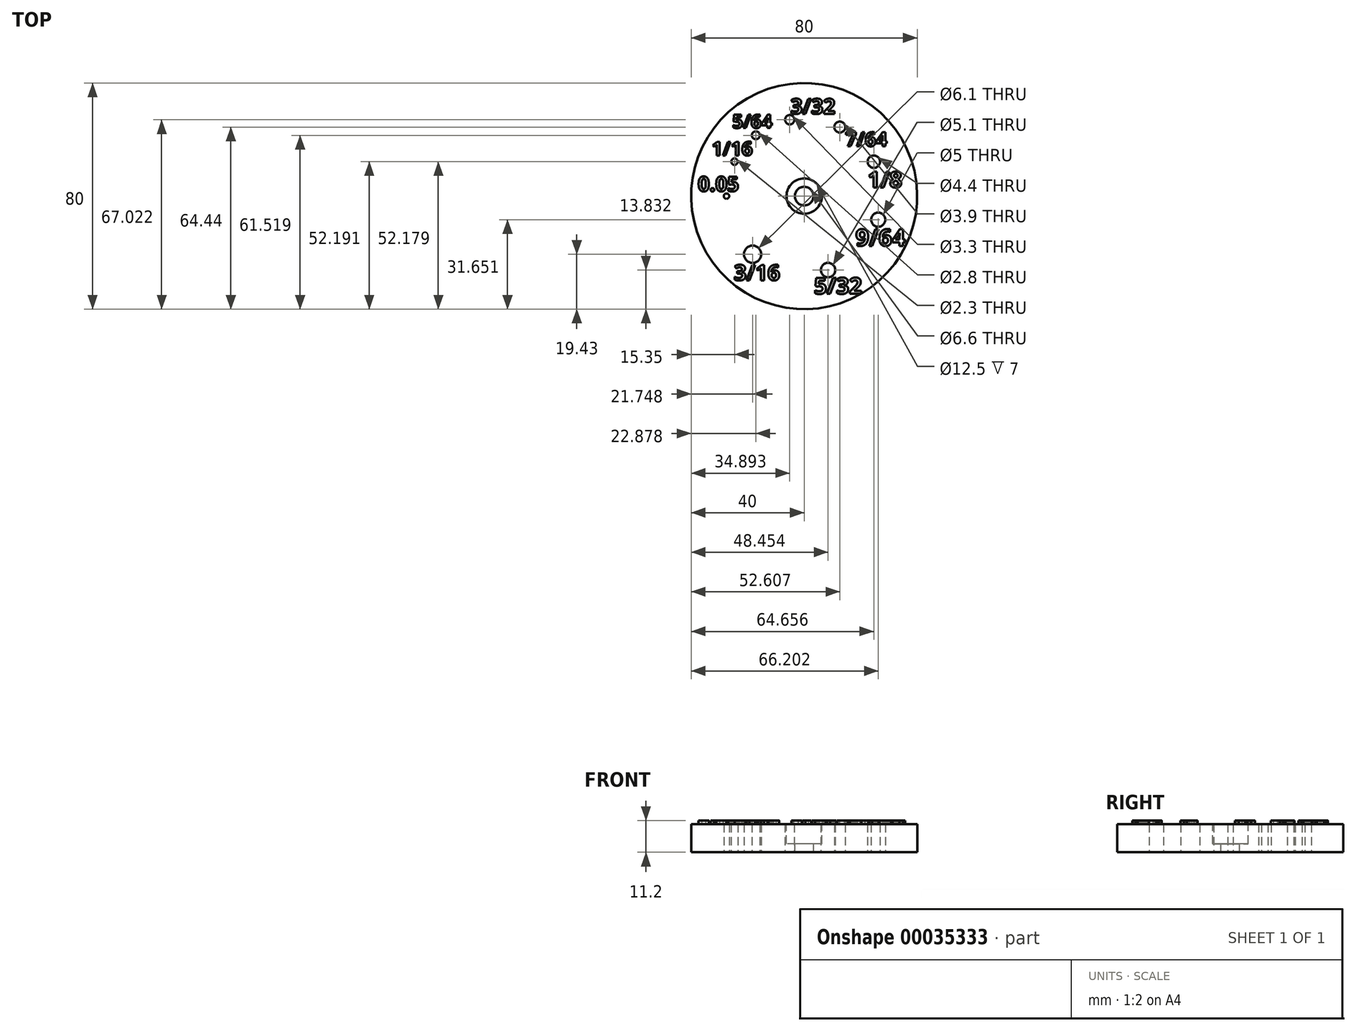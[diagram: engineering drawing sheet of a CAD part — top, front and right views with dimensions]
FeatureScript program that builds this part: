
annotation { "Feature Type Name" : "Feature", "Feature Type Description" : "" }
export const myFeature = defineFeature(function(context is Context, id is Id, definition is map)
    precondition{}
    {
        {
            var Q0;
            Q0=qCreatedBy(makeId("Top.planeOp"),FACE);
            var sketch = newSketch(context, id + "F0", { "sketchPlane" : qUnion([Q0])});
            skCircle(sketch, "E0", {"center": v(0, 0) * mm, "radius": 40 * mm});
            skCircle(sketch, "E1", {"center": v(-18.25, -20.57) * mm, "radius": 3.05 * mm});
            skCircle(sketch, "E2", {"center": v(8.45, -26.17) * mm, "radius": 2.55 * mm});
            skCircle(sketch, "E3", {"center": v(26.2, -8.35) * mm, "radius": 2.5 * mm});
            skCircle(sketch, "E4", {"center": v(24.66, 12.18) * mm, "radius": 2.2 * mm});
            skCircle(sketch, "E5", {"center": v(12.6, 24.44) * mm, "radius": 1.95 * mm});
            skCircle(sketch, "E6", {"center": v(-5.1, 27.02) * mm, "radius": 1.65 * mm});
            skCircle(sketch, "E7", {"center": v(-17.12, 21.52) * mm, "radius": 1.4 * mm});
            skCircle(sketch, "E8", {"center": v(-24.65, 12.2) * mm, "radius": 1.15 * mm});
            skCircle(sketch, "E9", {"center": v(-27.5, 0) * mm, "radius": 0.95 * mm});
            skCircle(sketch, "E10", {"center": v(0, 0) * mm, "radius": 27.5 * mm, "construction": true});
            skCircle(sketch, "E11", {"center": v(-18.25, -20.57) * mm, "radius": 13 * mm, "construction": true});
            skCircle(sketch, "E12", {"center": v(8.45, -26.17) * mm, "radius": 13 * mm, "construction": true});
            skCircle(sketch, "E13", {"center": v(26.2, -8.35) * mm, "radius": 10 * mm, "construction": true});
            skCircle(sketch, "E14", {"center": v(24.66, 12.18) * mm, "radius": 8 * mm, "construction": true});
            skCircle(sketch, "E15", {"center": v(12.6, 24.44) * mm, "radius": 7 * mm, "construction": true});
            skSolve(sketch);
        }
        {
            var Q0;
            Q0=makeQuery(id+"F0.imprint","IMPRINT",FACE,{"disambiguationData":[TD([[makeQuery(id+"F0.imprint","IMPRINT",EDGE,{"derivedFrom":sQuery(id+"F0.wireOp",EDGE,"E0")}),1.0]])]});
            extrude(context, id + "F1", {"entities" : qUnion([Q0]), "depth" : 10 * mm});
        }
        {
            var Q0;
            Q0=makeQuery(id+"F1.opExtrude","CAP_FACE",FACE,{"disambiguationData":[OSD([sQuery(id+"F0.wireOp",EDGE,"E0"),sQuery(id+"F0.wireOp",EDGE,"E1"),sQuery(id+"F0.wireOp",EDGE,"E2"),sQuery(id+"F0.wireOp",EDGE,"E3"),sQuery(id+"F0.wireOp",EDGE,"E4"),sQuery(id+"F0.wireOp",EDGE,"E5"),sQuery(id+"F0.wireOp",EDGE,"E6"),sQuery(id+"F0.wireOp",EDGE,"E7"),sQuery(id+"F0.wireOp",EDGE,"E8"),sQuery(id+"F0.wireOp",EDGE,"E9"),sQuery(id+"F0.wireOp",EDGE,"0fb7586f-180d-4d35-86ce-f1a024c8a606")])],"isStart":false});
            var sketch = newSketch(context, id + "F2", { "sketchPlane" : qUnion([Q0])});
            skText(sketch, "E16", { "text": "3/16", "fontName": "OpenSans-Bold.ttf"});
            skText(sketch, "E17", { "text": "5/32", "fontName": "OpenSans-Bold.ttf"});
            skText(sketch, "E18", { "text": "9/64", "fontName": "OpenSans-Bold.ttf"});
            skText(sketch, "E19", { "text": "1/8", "fontName": "OpenSans-Bold.ttf"});
            skText(sketch, "E20", { "text": "7/64", "fontName": "OpenSans-Bold.ttf"});
            skText(sketch, "E21", { "text": "3/32", "fontName": "OpenSans-Bold.ttf"});
            skText(sketch, "E22", { "text": "5/64", "fontName": "OpenSans-Bold.ttf"});
            skText(sketch, "E23", { "text": "1/16", "fontName": "OpenSans-Bold.ttf"});
            skText(sketch, "E24", { "text": "0.05", "fontName": "OpenSans-Bold.ttf"});
            const initialGuessF2  = {"E16": [-0.02483, -0.0298, 1, 0, 0.0055], "E17": [0.0035, -0.03459, 1, 0, 0.00574], "E18": [0.0182, -0.01762, 1, 0, 0.00597], "E19": [0.0225, 0.00306, 1, 0, 0.00562], "E20": [0.0146, 0.01764, 1, 0, 0.00502], "E21": [-0.00487, 0.0291, 1, 0, 0.00538], "E22": [-0.02543, 0.02409, 1, 0, 0.00478], "E23": [-0.03273, 0.01438, 1, 0, 0.0049], "E24": [-0.03763, 0.0017, 1, 0, 0.00524]};
            skSetInitialGuess(sketch, initialGuessF2);
            skSolve(sketch);
        }
        {
            var Q0;
            Q0 = qSketchRegion(id + "F2", true);
            extrude(context, id + "F3", {"entities" : qUnion([Q0]), "operationType" : NewBodyOperationType.ADD, "depth" : 1.2 * mm});
        }
        {
            var Q0;
            {var subQ0=sQuery(id+"F0.wireOp",EDGE,"E0");var subQ1=sQuery(id+"F0.wireOp",EDGE,"E1");var subQ2=sQuery(id+"F0.wireOp",EDGE,"E2");var subQ3=sQuery(id+"F0.wireOp",EDGE,"E3");var subQ4=sQuery(id+"F0.wireOp",EDGE,"E4");var subQ5=sQuery(id+"F0.wireOp",EDGE,"E5");var subQ6=sQuery(id+"F0.wireOp",EDGE,"E6");var subQ7=sQuery(id+"F0.wireOp",EDGE,"E7");var subQ8=sQuery(id+"F0.wireOp",EDGE,"E8");var subQ9=sQuery(id+"F0.wireOp",EDGE,"E9");Q0=makeQuery(id+"F3.boolean.opBoolean","SPLIT",FACE,{"disambiguationData":[TD([makeQuery(id+"F1.opExtrude","SWEPT_FACE",FACE,{"disambiguationData":[OSD([subQ0])]})])],"derivedFrom":makeQuery(id+"F1.opExtrude","CAP_FACE",FACE,{"disambiguationData":[OSD([subQ0,subQ1,subQ2,subQ3,subQ4,subQ5,subQ6,subQ7,subQ8,subQ9])],"isStart":false})});}
            var sketch = newSketch(context, id + "F4", { "sketchPlane" : qUnion([Q0])});
            skPoint(sketch, "E25", {"position": v(0, 0) * mm});
            skSolve(sketch);
        }
        {
            var Q0;
            Q0=sQuery(id+"F4.wireOp",VERTEX,"E25");
            var Q1;
            Q1=makeQuery(id+"F1.opExtrude","SWEPT_BODY",BODY,{"disambiguationData":[OSD([sQuery(id+"F0.wireOp",EDGE,"E0"),sQuery(id+"F0.wireOp",EDGE,"E1"),sQuery(id+"F0.wireOp",EDGE,"E2"),sQuery(id+"F0.wireOp",EDGE,"E3"),sQuery(id+"F0.wireOp",EDGE,"E4"),sQuery(id+"F0.wireOp",EDGE,"E5"),sQuery(id+"F0.wireOp",EDGE,"E6"),sQuery(id+"F0.wireOp",EDGE,"E7"),sQuery(id+"F0.wireOp",EDGE,"E8"),sQuery(id+"F0.wireOp",EDGE,"E9")])]});
            hole(context, id + "F5", {"style" : HoleStyle.C_BORE, "holeDiameter" : 6.6 * mm, "cBoreDiameter" : 12.5 * mm, "cBoreDepth" : 7 * mm, "endStyle" : HoleEndStyle.THROUGH, "locations" : qUnion([Q0]), "scope" : qUnion([Q1])});
        }
    });
